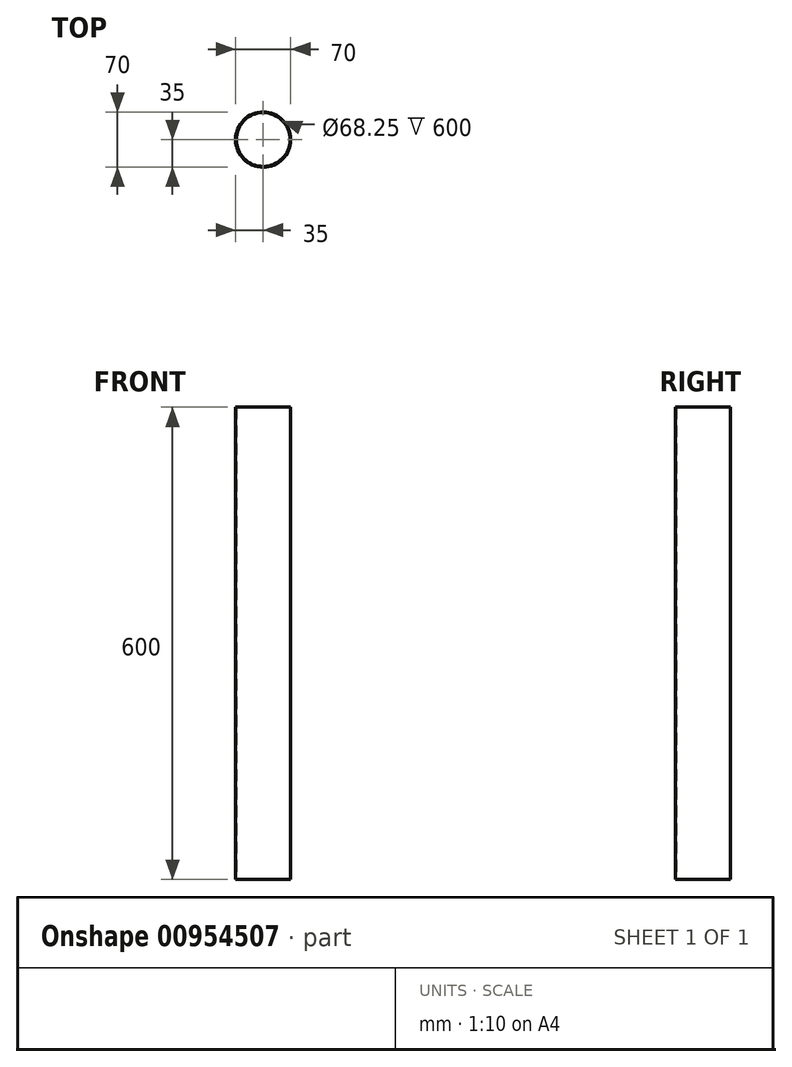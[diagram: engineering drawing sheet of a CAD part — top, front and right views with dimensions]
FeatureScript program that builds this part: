
annotation { "Feature Type Name" : "Feature", "Feature Type Description" : "" }
export const myFeature = defineFeature(function(context is Context, id is Id, definition is map)
    precondition{}
    {
        {
            var Q0;
            Q0=qCreatedBy(makeId("Top.planeOp"),FACE);
            var sketch = newSketch(context, id + "F0", { "sketchPlane" : qUnion([Q0])});
            skCircle(sketch, "E0", {"center": v(0, 0) * mm, "radius": 35 * mm});
            skCircle(sketch, "E1", {"center": v(0, 0) * mm, "radius": 34.12 * mm});
            skSolve(sketch);
        }
        {
            var Q0;
            Q0 = qSketchRegion(id + "F0", true);
            extrude(context, id + "F1", {"entities" : qUnion([Q0]), "depth" : 600 * mm, "offsetDistance" : 25 * mm});
        }
    });
